# Revit family: VFO
name_source: partatom
category: Air Terminals
revit_build: Autodesk Revit MEP 2012 (Build: 20110309_2315(x64)
units: mm (PartAtom-declared; Revit-internal decimal feet)

## types (3) — shared parameters
B Plato = 23 3/4"
C = 2 15/16"
C1 = 1 7/16"
D = 21 3/4"
Máxima presión estática = 0.00 in-wg
Mínima presión estática = 0.00 in-wg

## per-type parameters (varying)
| type | A Cuello | A1 | A2 | A4 | C original | C2 original | M | Manufacturer | Material | Max Flow | Min Flow | Máxima velocidad de cuello | Máximo nivel de ruido (NC) | Mínima velocidad de cuello | URL |
| VFO-R-06 | 6" | 13" | 14 1/2" | 3" | 21 7/16" | 13 7/8" | 2 1/2" | INNES | Aluminio/Acero | 280 CFM | 60 CFM | 300 FPM | 34 | 1400 FPM | http://www.innes.com.mx |
| VFO-R-08 | 8" | 15" | 16 1/2" | 4" | 21 3/4" | 13" | 4 1/2" |  |  | 0 CFM | 0 CFM | 0 FPM |  | 0 FPM |  |
| VFO-R-10 | 10" | 17" | 18 1/2" | 5" | 21 3/4" | 13" | 6 1/2" |  |  | 0 CFM | 0 CFM | 0 FPM |  | 0 FPM |  |

## geometry (parser evidence)
native form markers: Sweep x1
no freeform markers — native parametric forms only
